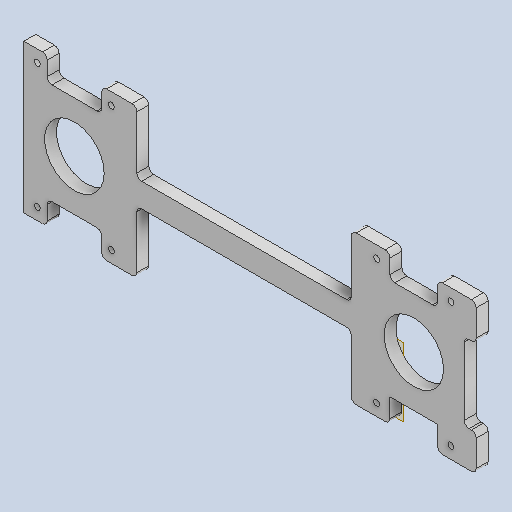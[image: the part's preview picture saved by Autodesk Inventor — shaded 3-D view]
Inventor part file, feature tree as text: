
AUTODESK INVENTOR PART (.ipt)
format: ipt  version: 2022 (Build 260153000, 153)  size: 593,920 bytes
history: native  units: mm
features: reference x14, extrude x8, sketch x7, fillet x5, other x4, projected_geometry x2, plane x1
ambient origin geometry x8: Origin, YZ Plane, XZ Plane, XY Plane, X Axis, Y Axis, Z Axis, Center Point
bodies: Solid1 (feature_tree)
feature tree (41):
  extrude  "Extrusion1"  Depth=5.0mm TaperAngle=0.0deg
  fillet  "Fillet1"  Radius=2.0mm
  extrude  "Extrusion2"  Depth=10.0mm
  plane  "Work Plane1"
  extrude  "Extrusion3"  Depth=25.0mm
  sketch  "Sketch4"  dims[d9=5.0mm d10=0.0mm d11=6.0mm]
  extrude  "Extrusion4"  Depth=6.0mm
  extrude  "Extrusion5"  Depth=3.0mm
  extrude  "Extrusion14"  Depth=3.0mm
  extrude  "Extrusion15"  TaperAngle=90.0deg  [1 undecoded]
  fillet  "Fillet2"  Radius=3.0mm
  fillet  "Fillet3"  Radius=3.0mm
  fillet  "Fillet4"  Radius=3.0mm
  fillet  "Fillet5"  Radius=1.0mm
  extrude  "Extrusion16"  Depth=2.0mm
  sketch  "Sketch1"  dims[d0=25.0mm d1=5.0mm d2=0.0mm d3=2.0mm]
  reference  "Reference1"
  reference  "Reference2"
  reference  "Reference3"
  sketch  "Sketch2"  dims[d4=5.0mm d5=10.0mm]
  reference  "Reference4"
  sketch  "Sketch3"  dims[d6=100.0mm d7=0.0mm d8=25.0mm]
  reference  "Reference5"
  reference  "Reference6"
  reference  "Reference7"
  reference  "Reference8"
  reference  "Reference9"
  sketch  "Sketch5"  dims[d12=100.0mm d13=3.0mm]
  projected_geometry  "Projected Loop1"
  sketch  "Sketch17"  dims[d15=90.0deg d18=3.0mm]
  projected_geometry  "Projected Loop14"
  sketch  "Sketch18"  dims[d20=3.0mm d21=90.0deg d22=3.0mm d23=3.0mm d24=3.0mm d25=0.0mm d26=1.0mm d27=2.0mm d28=3.0mm d29=10.0mm d30=3.0mm d31=10.0mm d32=3.0mm d33=10.0mm d34=3.0mm d35=10.0mm d36=3.0mm d37=10.0mm d38=3.0mm d39=10.0mm d40=3.0mm d41=3.0mm d42=6.0mm d43=0.0mm d77=1.0mm d78=15.0mm d79=5.0mm d80=3.0mm d81=0.0mm d82=4.0mm d83=30.0mm d84=5.0mm d85=20.0mm d86=5.0mm d87=20.0mm d88=10.0mm d89=5.0mm d90=90.0deg d91=5.0mm d92=3.0mm d93=0.0mm d94=2.0mm d95=2.0mm d96=2.0mm d97=2.0mm d98=10.0mm d99=10.0mm d100=1.0mm d101=0.0mm]
  reference  "Reference12"
  reference  "Reference13"
  reference  "Reference14"
  reference  "Reference15"
  reference  "Reference16"
  other  "<userpath>\OneDrive\Namizje\school\3. letnik\ZOPp\laserski merilnik\3d model\Assembly1.iam"
  other  "Assembly1.iam"
  other  "Hold of motors:1"
  other  "zaponka za motorje:1"
note: 1 required parameter value undecoded (feature->parameter linkage not recoverable at this tier; creation-order binding heuristic only, values carry confidence <= 0.55)
